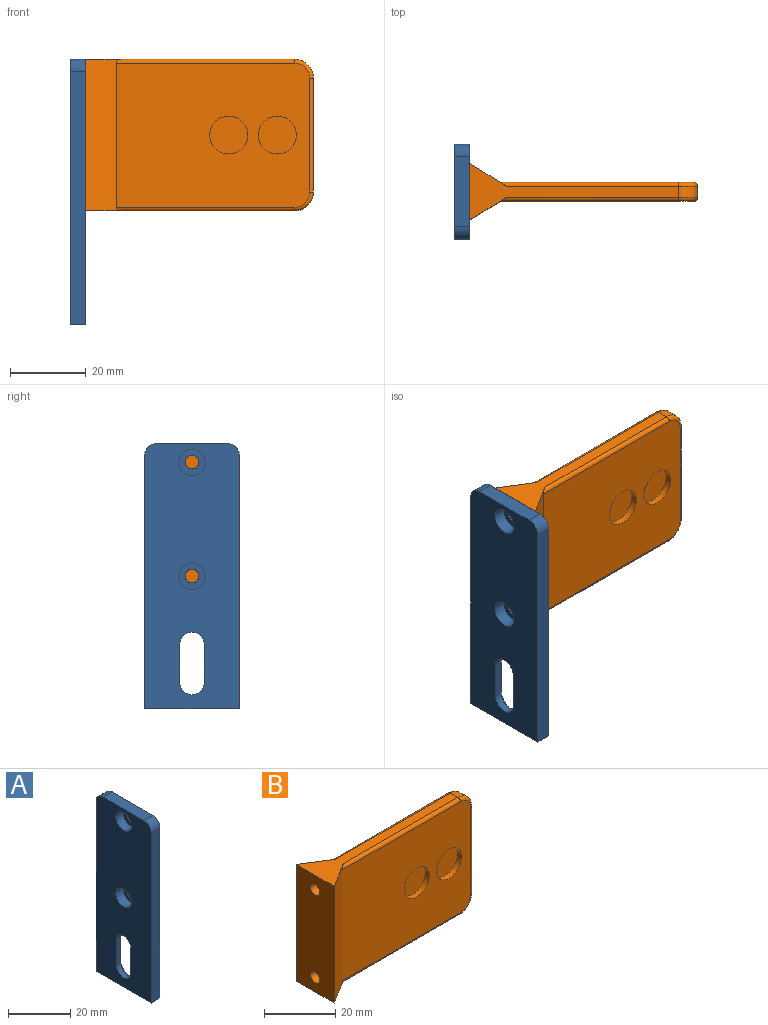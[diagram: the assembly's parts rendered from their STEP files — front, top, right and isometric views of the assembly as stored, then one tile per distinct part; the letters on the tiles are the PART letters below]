
ASSEMBLY  parts=2 mates=1
PART A: 23 faces, bbox 4x25x70 mm
  f0: cylinder r=1.8mm len=3.6mm, axis (1,0,0), area 7.9mm2, adj f2,f21
  f1: cylinder r=1.8mm len=3.6mm, axis (1,0,0), area 7.9mm2, adj f2,f19
  f2: plane 70x25mm, normal (1,0,0), area 1511.7mm2, adj f0,f1,f7,f8,f9,f10,f12,f13
  f3: plane 10x2mm, normal (0,1,0), area 20mm2, adj f4,f5,f11,f16
  f4: cylinder r=3.25mm len=6.5mm, axis (1,0,0), area 20.4mm2, adj f3,f6,f11,f16
  f5: cylinder r=3.25mm len=6.5mm, axis (1,0,0), area 20.4mm2, adj f3,f6,f11,f16
  f6: plane 10x2mm, normal (0,-1,0), area 20mm2, adj f4,f5,f11,f16
  f7: plane 18.4x4mm, normal (0,0,1), area 73.6mm2, adj f2,f11,f17,f18
  f8: plane 66.7x4mm, normal (0,-1,0), area 266.8mm2, adj f2,f9,f11,f17
  f9: plane 25x4mm, normal (0,0,-1), area 100mm2, adj f2,f8,f10,f11
  f10: plane 66.7x4mm, normal (0,1,0), area 266.8mm2, adj f2,f9,f11,f18
  f11: plane 70x25mm, normal (-1,0,0), area 1570.2mm2, adj f3,f4,f5,f6,f7,f8,f9,f10
  f12: plane 10x2mm, normal (0,-1,0), area 20mm2, adj f2,f13,f15,f16
  f13: cylinder r=5.65mm len=11.3mm, axis (1,0,0), area 35.5mm2, adj f2,f12,f14,f16
  f14: plane 10x2mm, normal (0,1,0), area 20mm2, adj f2,f13,f15,f16
  f15: cylinder r=5.65mm len=11.3mm, axis (1,0,0), area 35.5mm2, adj f2,f12,f14,f16
  f16: plane 21.3x11.3mm, normal (1,0,0), area 115.1mm2, adj f3,f4,f5,f6,f12,f13,f14,f15
  f17: cylinder r=3.3mm len=4mm, axis (1,0,0), area 20.7mm2, adj f2,f7,f8,f11
  f18: cylinder r=3.3mm len=4mm, axis (-1,0,0), area 20.7mm2, adj f2,f7,f10,f11
  f19: plane 7x7mm, normal (-1,0,0), area 28.3mm2, adj f1,f20
  f20: cylinder r=3.5mm len=7mm, axis (-1,0,0), area 72.6mm2, adj f11,f19
  f21: plane 7x7mm, normal (-1,0,0), area 28.3mm2, adj f0,f22
  f22: cylinder r=3.5mm len=7mm, axis (-1,0,0), area 72.6mm2, adj f11,f21
PART B: 28 faces, bbox 60.4x15x40.8 mm
  f0: plane 51x38mm, normal (0,1,0), area 1931.1mm2, adj f7,f23,f24,f25,f26,f27
  f1: plane 51x38mm, normal (0,-1,0), area 1774.1mm2, adj f6,f8,f10,f18,f19,f20,f21,f22
  f2: plane 30x3mm, normal (1,0,0), area 90mm2, adj f16,f17,f20,f25
  f3: plane 55x15mm, normal (0,0,1), area 222.6mm2, adj f4,f6,f7,f16,f18,f23
  f4: plane 40x15mm, normal (-1,0,0), area 578.5mm2, adj f3,f5,f6,f7,f12,f14
  f5: plane 55x15mm, normal (0,0,-1), area 222.6mm2, adj f4,f6,f7,f17,f22,f27
  f6: plane 40x9.6mm, normal (0.53,-0.85,0), area 378.2mm2, adj f1,f3,f4,f5,f18,f22
  f7: plane 40x9.6mm, normal (0.53,0.85,0), area 378.2mm2, adj f0,f3,f4,f5,f23,f27
  f8: cylinder r=5mm len=10mm, axis (0,-1,0), area 53.4mm2, adj f1,f9
  f9: plane 10x10mm, normal (0,-1,0), area 78.5mm2, adj f8
  f10: cylinder r=5mm len=10mm, axis (0,-1,0), area 53.4mm2, adj f1,f11
  f11: plane 10x10mm, normal (0,-1,0), area 78.5mm2, adj f10
  f12: cylinder r=1.85mm len=52mm, axis (-1,0,0), area 604.4mm2, adj f4,f13
  f13: plane 3.7x3.7mm, normal (-1,0,0), area 10.8mm2, adj f12
  f14: cylinder r=1.85mm len=52mm, axis (-1,0,0), area 604.4mm2, adj f4,f15
  f15: plane 3.7x3.7mm, normal (-1,0,0), area 10.8mm2, adj f14
  f16: cylinder r=5mm len=5mm, axis (0,-1,0), area 23.6mm2, adj f2,f3,f19,f24
  f17: cylinder r=5mm len=5mm, axis (0,1,0), area 23.6mm2, adj f2,f5,f21,f26
  f18: cylinder r=1mm len=47mm, axis (1,0,0), area 72.9mm2, adj f1,f3,f6,f19
  f19: torus R=4mm, axis (0,-1,0), area 11.4mm2, adj f1,f16,f18,f20
  f20: cylinder r=1mm len=30mm, axis (0,0,-1), area 47.1mm2, adj f1,f2,f19,f21
  f21: torus R=4mm, axis (0,-1,0), area 11.4mm2, adj f1,f17,f20,f22
  f22: cylinder r=1mm len=47mm, axis (-1,0,0), area 72.9mm2, adj f1,f5,f6,f21
  f23: cylinder r=1mm len=47mm, axis (-1,0,0), area 72.9mm2, adj f0,f3,f7,f24
  f24: torus R=4mm, axis (0,-1,0), area 11.4mm2, adj f0,f16,f23,f25
  f25: cylinder r=1mm len=30mm, axis (0,0,1), area 47.1mm2, adj f0,f2,f24,f26
  f26: torus R=4mm, axis (0,-1,0), area 11.4mm2, adj f0,f17,f25,f27
  f27: cylinder r=1mm len=47mm, axis (1,0,0), area 72.9mm2, adj f0,f5,f7,f26
PLACE A t=(-2.03,-0.44,0.86)mm fixed
PLACE B t=(31.97,2.06,15.86)mm
MATE fastened A.f1 <-> B.f14  axis (1,0,0) through (1.97,-0.44,30.86)mm
